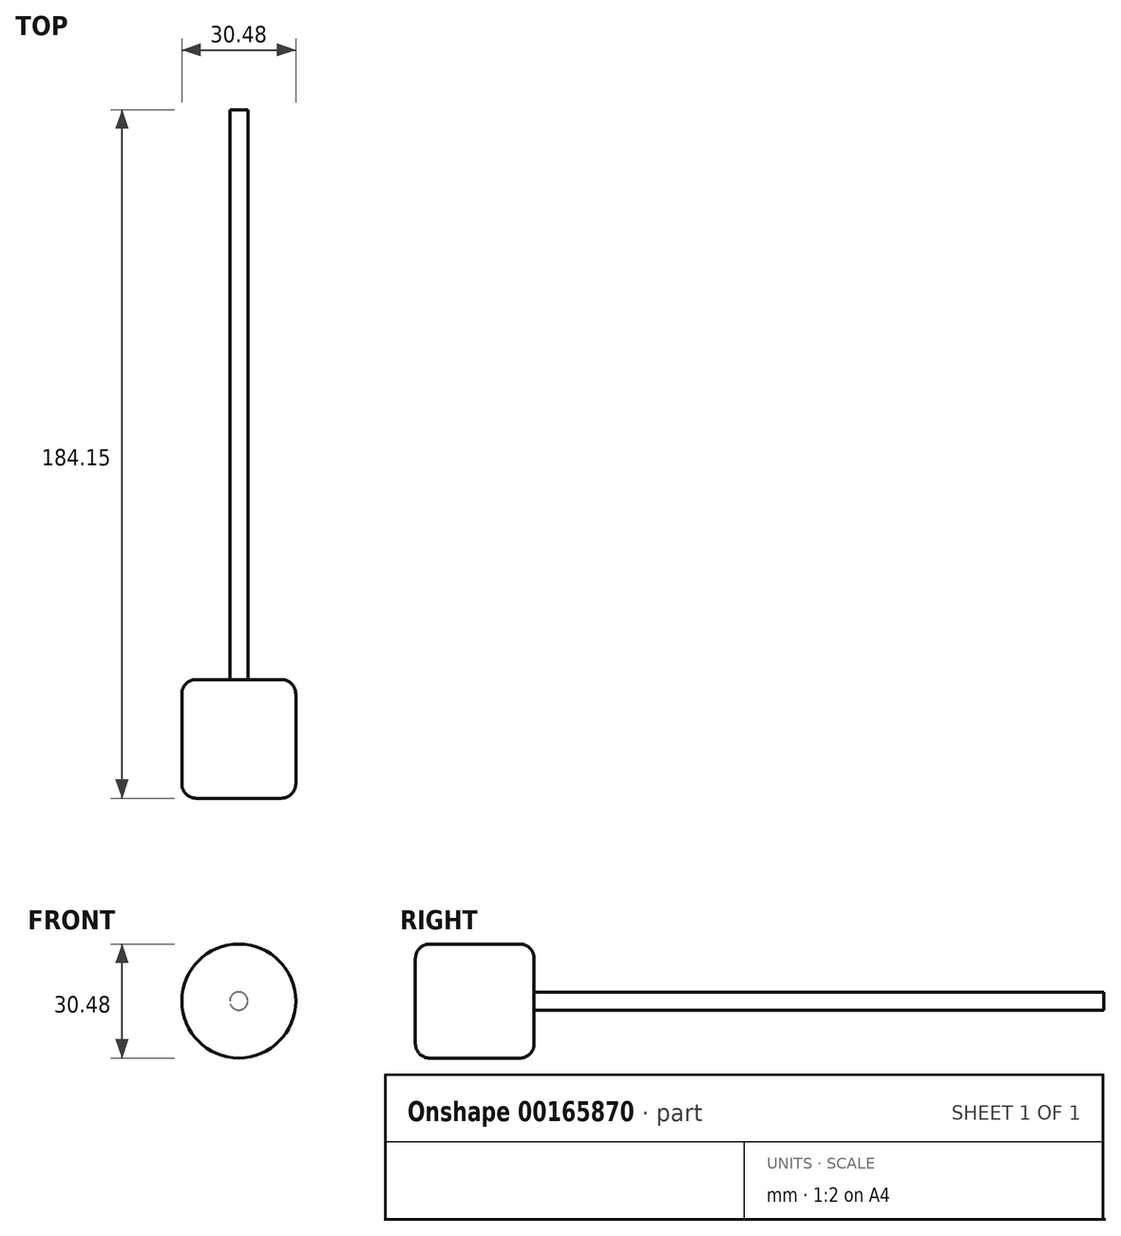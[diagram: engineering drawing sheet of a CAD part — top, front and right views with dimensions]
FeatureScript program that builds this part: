
annotation { "Feature Type Name" : "Feature", "Feature Type Description" : "" }
export const myFeature = defineFeature(function(context is Context, id is Id, definition is map)
    precondition{}
    {
        {
            var Q0;
            Q0=qCreatedBy(makeId("Front.planeOp"),FACE);
            var sketch = newSketch(context, id + "F0", { "sketchPlane" : qUnion([Q0])});
            skCircle(sketch, "E0", {"center": v(0, 0) * mm, "radius": 15.24 * mm});
            skSolve(sketch);
        }
        {
            var Q0;
            Q0 = qSketchRegion(id + "F0", true);
            extrude(context, id + "F1", {"entities" : qUnion([Q0]), "depth" : 31.75 * mm});
        }
        {
            var Q0;
            Q0=makeQuery(id+"F1.opExtrude","CAP_EDGE",EDGE,{"disambiguationData":[OSD([sQuery(id+"F0.wireOp",EDGE,"E0")])],"isStart":false});
            var Q1;
            Q1=makeQuery(id+"F1.opExtrude","CAP_EDGE",EDGE,{"disambiguationData":[OSD([sQuery(id+"F0.wireOp",EDGE,"E0")])],"isStart":true});
            fillet(context, id + "F2", {"entities" : qUnion([Q0, Q1]), "radius" : 3.8 * mm, "tangentPropagation" : true, "allowEdgeOverflow" : false});
        }
        {
            var Q0;
            Q0=makeQuery(id+"F1.opExtrude","CAP_FACE",FACE,{"disambiguationData":[OSD([sQuery(id+"F0.wireOp",EDGE,"E0")])],"isStart":true});
            var sketch = newSketch(context, id + "F3", { "sketchPlane" : qUnion([Q0])});
            skCircle(sketch, "E1", {"center": v(0, 0) * mm, "radius": 2.41 * mm});
            skSolve(sketch);
        }
        {
            var Q0;
            Q0 = qSketchRegion(id + "F3", true);
            extrude(context, id + "F4", {"entities" : qUnion([Q0]), "operationType" : NewBodyOperationType.ADD, "depth" : 152.4 * mm});
        }
    });
